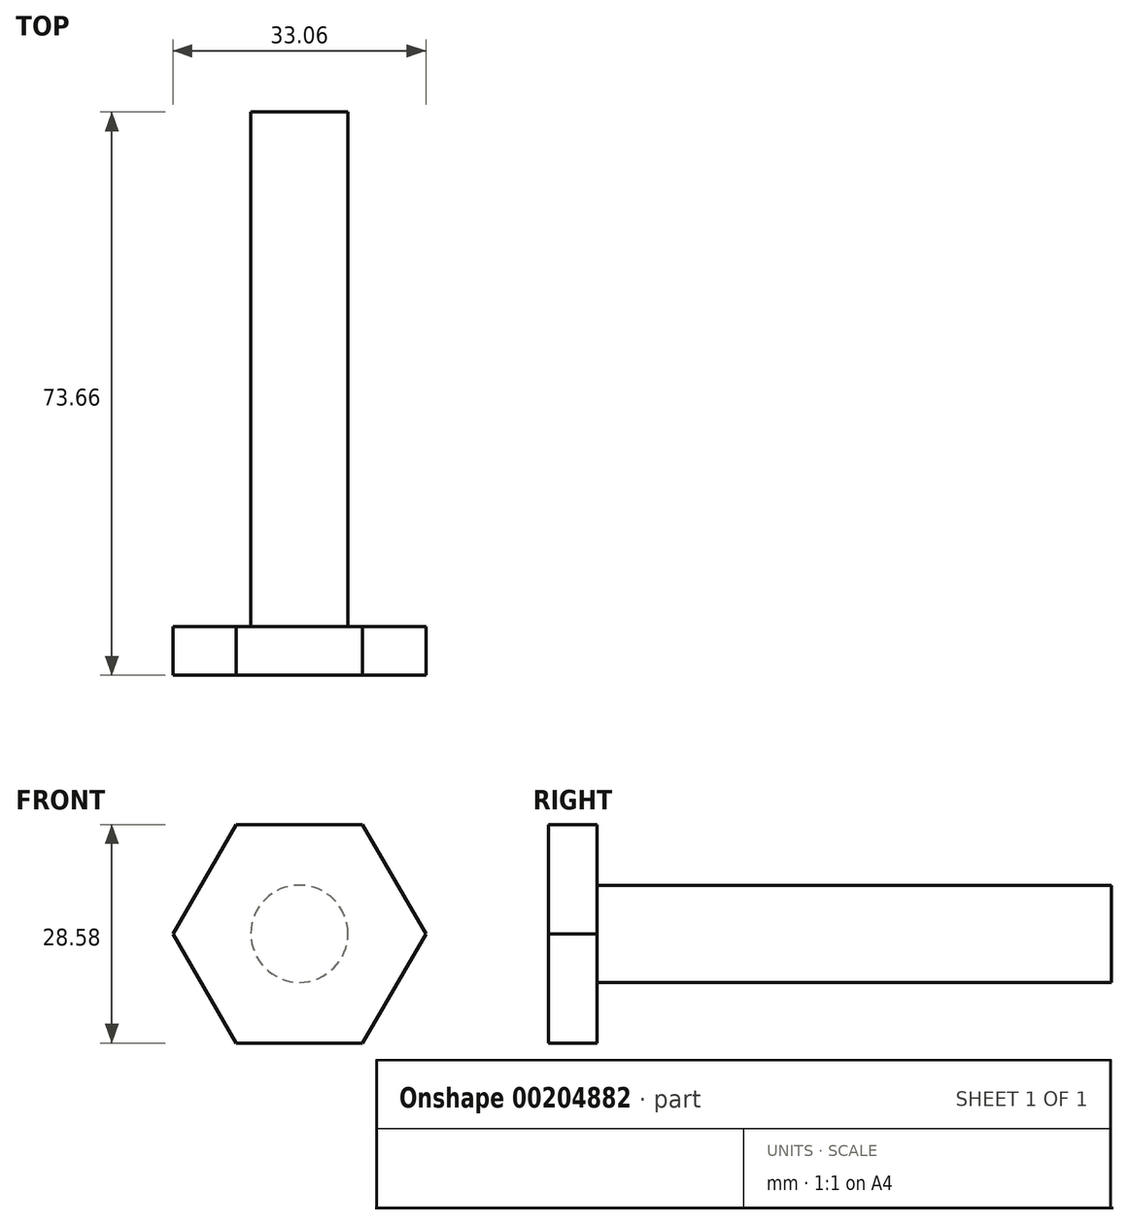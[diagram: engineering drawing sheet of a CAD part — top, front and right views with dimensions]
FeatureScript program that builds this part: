
annotation { "Feature Type Name" : "Feature", "Feature Type Description" : "" }
export const myFeature = defineFeature(function(context is Context, id is Id, definition is map)
    precondition{}
    {
        {
            var Q0;
            Q0=qCreatedBy(makeId("Front.planeOp"),FACE);
            var sketch = newSketch(context, id + "F0", { "sketchPlane" : qUnion([Q0])});
            skCircle(sketch, "E0", {"center": v(0, 0) * mm, "radius": 6.35 * mm});
            skSolve(sketch);
        }
        {
            var Q0;
            Q0 = qSketchRegion(id + "F0", true);
            extrude(context, id + "F1", {"entities" : qUnion([Q0]), "oppositeDirection" : true, "depth" : 67.3 * mm});
        }
        {
            var Q0;
            Q0=makeQuery(id+"F1.opExtrude","CAP_FACE",FACE,{"disambiguationData":[OSD([sQuery(id+"F0.wireOp",EDGE,"E0")])],"isStart":true});
            var sketch = newSketch(context, id + "F2", { "sketchPlane" : qUnion([Q0])});
            skLineSegment(sketch, "E1", {"start": v(-16.53, 0) * mm, "end": v(-8.26, 14.29) * mm});
            skLineSegment(sketch, "E2", {"start": v(-8.26, 14.29) * mm, "end": v(8.26, 14.29) * mm});
            skLineSegment(sketch, "E3", {"start": v(8.26, 14.29) * mm, "end": v(16.53, 0) * mm});
            skLineSegment(sketch, "E4", {"start": v(16.53, 0) * mm, "end": v(8.25, -14.29) * mm});
            skLineSegment(sketch, "E5", {"start": v(8.26, -14.29) * mm, "end": v(-8.26, -14.29) * mm});
            skLineSegment(sketch, "E6", {"start": v(-8.25, -14.29) * mm, "end": v(-16.53, 0) * mm});
            skSolve(sketch);
        }
        {
            var Q0;
            Q0 = qSketchRegion(id + "F2", true);
            extrude(context, id + "F3", {"entities" : qUnion([Q0]), "operationType" : NewBodyOperationType.ADD, "depth" : 6.35 * mm});
        }
    });
